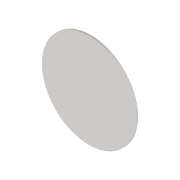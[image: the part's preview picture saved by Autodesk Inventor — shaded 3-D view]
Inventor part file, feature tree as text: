
AUTODESK INVENTOR PART (.ipt)
format: ipt  version: 2021 (Build 250183000, 183)  size: 74,752 bytes
history: native  units: mm
features: extrude x1, sketch x1
ambient origin geometry x8: Origin, YZ Plane, XZ Plane, XY Plane, X Axis, Y Axis, Z Axis, Center Point
bodies: Solid1 (feature_tree)
feature tree (2):
  extrude  "Extrusion1"  Depth=1.0mm TaperAngle=0.0deg
  sketch  "Sketch1"  dims[d0=50.0mm d1=1.0mm d2=0.0mm]
